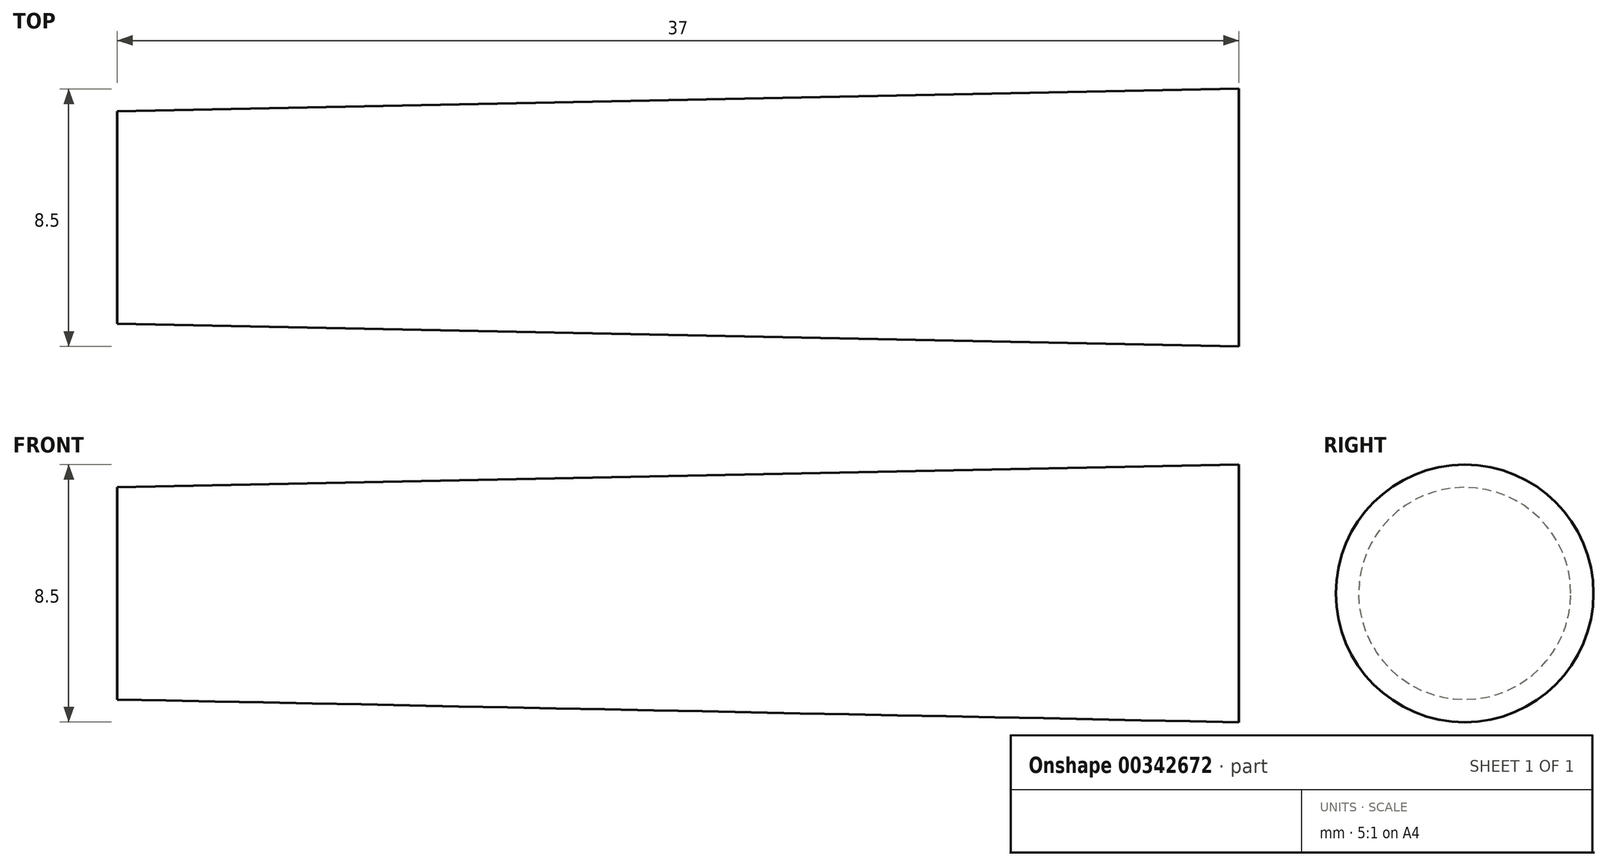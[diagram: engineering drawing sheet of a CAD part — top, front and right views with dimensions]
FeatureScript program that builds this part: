
annotation { "Feature Type Name" : "Feature", "Feature Type Description" : "" }
export const myFeature = defineFeature(function(context is Context, id is Id, definition is map)
    precondition{}
    {
        {
            var Q0;
            Q0=qCreatedBy(makeId("Right.planeOp"),FACE);
            cPlane(context, id + "F0", {"entities" : qUnion([Q0]), "cplaneType" : CPlaneType.OFFSET, "offset" : 7 * mm, "width" : 150 * mm, "height" : 150 * mm});
        }
        {
            var Q0;
            Q0=qCreatedBy(makeId("Right.planeOp"),FACE);
            cPlane(context, id + "F1", {"entities" : qUnion([Q0]), "cplaneType" : CPlaneType.OFFSET, "offset" : 30 * mm, "oppositeDirection" : true, "width" : 150 * mm, "height" : 150 * mm});
        }
        {
            var Q0;
            Q0=qCreatedBy(id+"F1.planeOp",FACE);
            var sketch = newSketch(context, id + "F2", { "sketchPlane" : qUnion([Q0])});
            skCircle(sketch, "E0", {"center": v(-44.28, 44.77) * mm, "radius": 3.5 * mm});
            skSolve(sketch);
        }
        {
            var Q0;
            Q0=qCreatedBy(id+"F0.planeOp",FACE);
            var sketch = newSketch(context, id + "F3", { "sketchPlane" : qUnion([Q0])});
            skCircle(sketch, "E1", {"center": v(-44.28, 44.77) * mm, "radius": 4.25 * mm});
            skSolve(sketch);
        }
        {
            var Q0;
            Q0=makeQuery(id+"F3.imprint","IMPRINT",FACE,{"disambiguationData":[TD([[makeQuery(id+"F3.imprint","IMPRINT",EDGE,{"derivedFrom":sQuery(id+"F3.wireOp",EDGE,"E1")}),1.0]])]});
            var Q1;
            Q1=makeQuery(id+"F2.imprint","IMPRINT",FACE,{"disambiguationData":[TD([[makeQuery(id+"F2.imprint","IMPRINT",EDGE,{"derivedFrom":sQuery(id+"F2.wireOp",EDGE,"E0")}),1.0]])]});
            loft(context, id + "F4", {"sheetProfilesArray" : [{ "sheetProfileEntities" : qUnion([Q0]) }, { "sheetProfileEntities" : qUnion([Q1]) }]});
        }
    });
